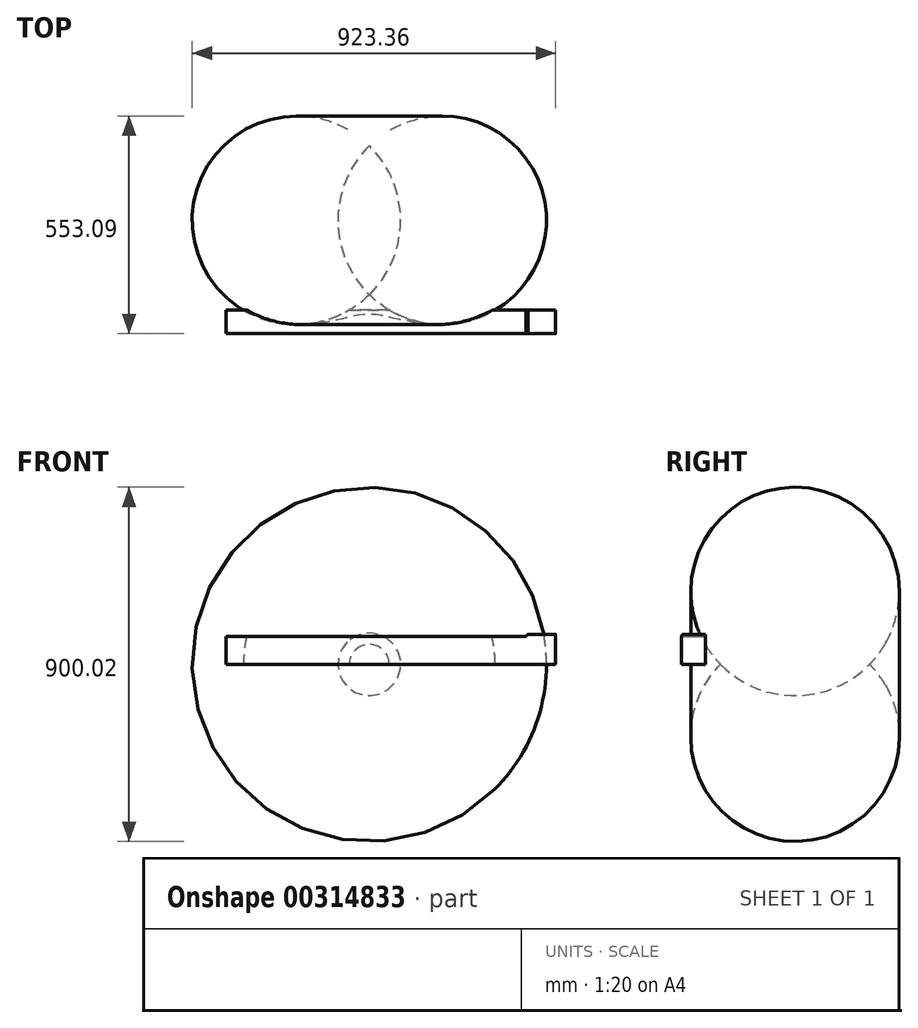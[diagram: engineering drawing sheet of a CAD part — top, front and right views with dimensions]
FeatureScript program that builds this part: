
annotation { "Feature Type Name" : "Feature", "Feature Type Description" : "" }
export const myFeature = defineFeature(function(context is Context, id is Id, definition is map)
    precondition{}
    {
        {
            var Q0;
            Q0=qCreatedBy(makeId("Top.planeOp"),FACE);
            var sketch = newSketch(context, id + "F0", { "sketchPlane" : qUnion([Q0])});
            skLineSegment(sketch, "E0.bottom", {"start": v(-62.15, 49.69) * mm, "end": v(13.51, 49.69) * mm});
            skLineSegment(sketch, "E0.top", {"start": v(-62.15, -10.36) * mm, "end": v(13.51, -10.36) * mm});
            skLineSegment(sketch, "E0.left", {"start": v(-62.15, 49.69) * mm, "end": v(-62.15, -10.36) * mm});
            skLineSegment(sketch, "E0.right", {"start": v(13.51, 49.69) * mm, "end": v(13.51, -10.36) * mm});
            skSolve(sketch);
        }
        {
            var Q0;
            Q0 = qSketchRegion(id + "F0", true);
            extrude(context, id + "F1", {"entities" : qUnion([Q0]), "depth" : 76.2 * mm});
        }
        {
            var Q0;
            Q0=makeQuery(id+"F1.opExtrude","CAP_EDGE",EDGE,{"disambiguationData":[OSD([sQuery(id+"F0.wireOp",EDGE,"E0.left")])],"isStart":false});
            chamfer(context, id + "F2", {"entities" : qUnion([Q0]), "width" : 5.08 * mm, "tangentPropagation" : true});
        }
        {
            var Q0;
            Q0=makeQuery(id+"F1.opExtrude","CAP_EDGE",EDGE,{"disambiguationData":[OSD([sQuery(id+"F0.wireOp",EDGE,"E0.top")])],"isStart":false});
            fillet(context, id + "F3", {"entities" : qUnion([Q0]), "radius" : 5.08 * mm, "tangentPropagation" : true, "allowEdgeOverflow" : false});
        }
        {
            var Q0;
            Q0=makeQuery(id+"F1.opExtrude","SWEPT_FACE",FACE,{"disambiguationData":[OSD([sQuery(id+"F0.wireOp",EDGE,"E0.left")])]});
            extrude(context, id + "F4", {"entities" : qUnion([Q0]), "operationType" : NewBodyOperationType.ADD, "depth" : 762 * mm});
        }
        {
            var Q0;
            Q0=qCreatedBy(makeId("Top.planeOp"),FACE);
            var sketch = newSketch(context, id + "F5", { "sketchPlane" : qUnion([Q0])});
            skLineSegment(sketch, "E1", {"start": v(-459.84, 88.5) * mm, "end": v(-459.84, 467.26) * mm});
            skArc(sketch, "E2", {"start": v(-459.84, 88.5) * mm, "mid": v(-9.84, 277.88) * mm, "end": v(-459.84, 467.26) * mm});
            skSolve(sketch);
        }
        {
            var Q0;
            Q0=makeQuery(id+"F5.imprint","IMPRINT",FACE,{"disambiguationData":[TD([[makeQuery(id+"F5.imprint","IMPRINT",EDGE,{"derivedFrom":sQuery(id+"F5.wireOp",EDGE,"E1")}),-1.0]])]});
            var Q1;
            Q1=sQuery(id+"F5.wireOp",EDGE,"E1");
            revolve(context, id + "F6", {"operationType" : NewBodyOperationType.ADD, "entities" : qUnion([Q0]), "axis" : qUnion([Q1]), "revolveType" : RevolveType.FULL});
        }
    });
